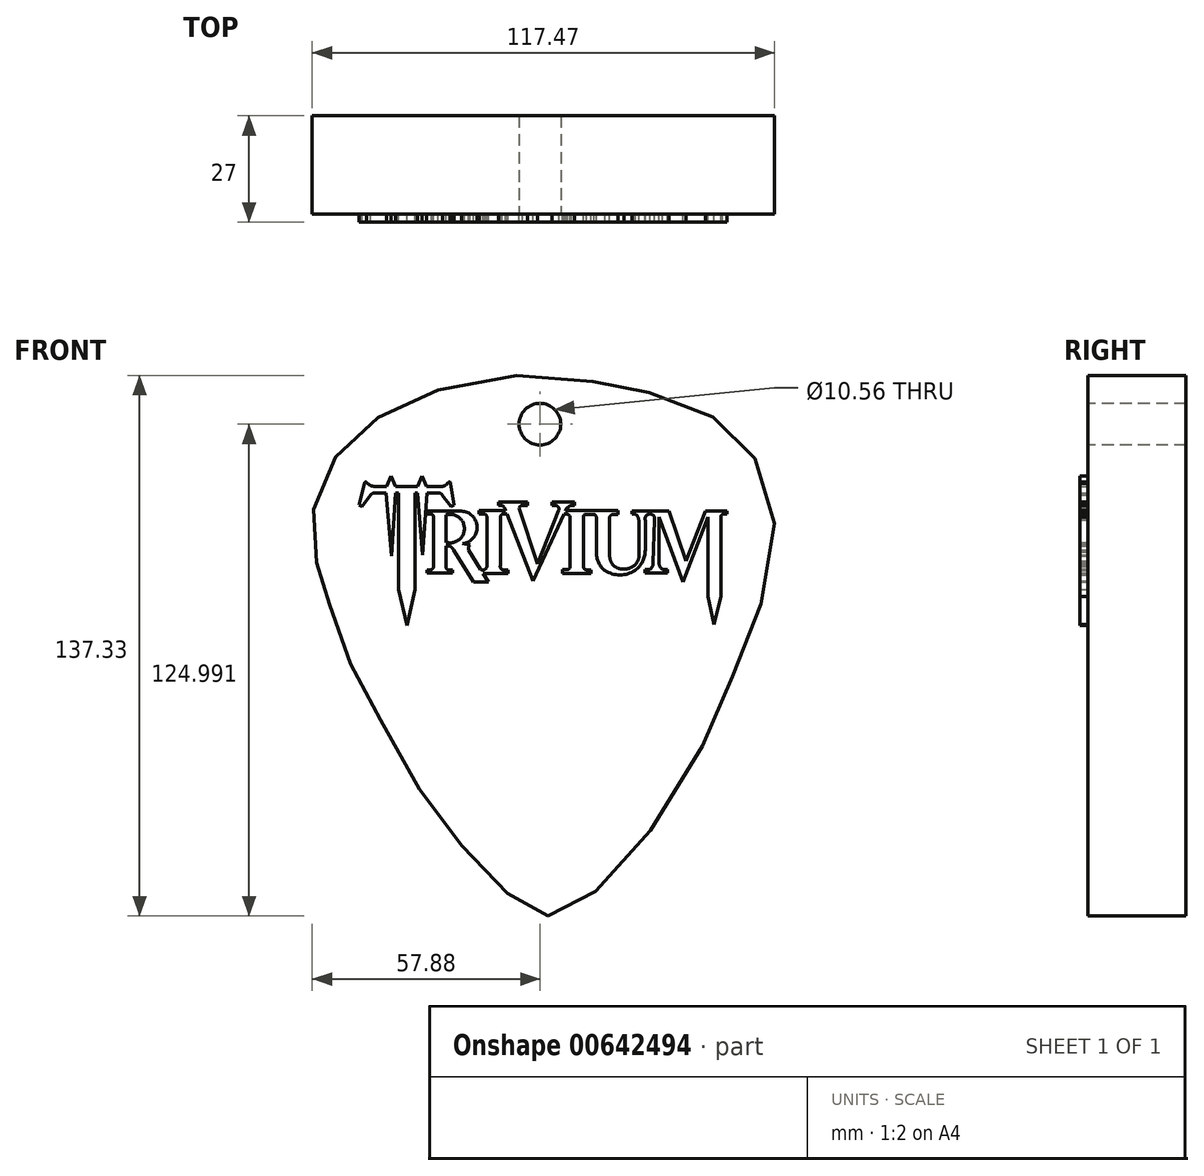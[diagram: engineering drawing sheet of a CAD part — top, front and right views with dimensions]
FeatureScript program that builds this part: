
annotation { "Feature Type Name" : "Feature", "Feature Type Description" : "" }
export const myFeature = defineFeature(function(context is Context, id is Id, definition is map)
    precondition{}
    {
        {
            var Q0;
            Q0=qCreatedBy(makeId("Front.planeOp"),FACE);
            var sketch = newSketch(context, id + "F0", { "sketchPlane" : qUnion([Q0])});
            skFitSpline(sketch, "E0", {"points": [v(1.98, -72.22) * mm, v(-3.4, -70.24) * mm, v(-13.31, -61.74) * mm, v(-24.07, -49) * mm, v(-35.12, -32.85) * mm, v(-45.03, -13.6) * mm, v(-49.85, -4.53) * mm, v(-54.38, 9.91) * mm, v(-56.15, 15.06) * mm, v(-57.8, 24.48) * mm, v(-56.74, 34.6) * mm, v(-51.16, 45.4) * mm, v(-42.15, 53.82) * mm, v(-28.73, 60.43) * mm, v(-7.1, 65.04) * mm, v(14.12, 63.43) * mm, v(25.14, 61.43) * mm, v(41.36, 56.02) * mm, v(51.37, 48.21) * mm, v(58.38, 35.8) * mm, v(58.18, 14.17) * mm, v(50.17, -8.06) * mm, v(42.96, -25.69) * mm, v(24.9, -54.7) * mm, v(10.37, -68.76) * mm, v(1.98, -72.22) * mm]});
            skSolve(sketch);
        }
        {
            var Q0;
            Q0=makeQuery(id+"F0.imprint","IMPRINT",FACE,{"disambiguationData":[TD([[makeQuery(id+"F0.imprint","IMPRINT",EDGE,{"derivedFrom":sQuery(id+"F0.wireOp",EDGE,"E0")}),-1.0]])]});
            extrude(context, id + "F1", {"entities" : qUnion([Q0]), "depth" : 25 * mm, "offsetDistance" : 25 * mm});
        }
        {
            var Q0;
            Q0=makeQuery(id+"F1.opExtrude","CAP_FACE",FACE,{"disambiguationData":[OSD([sQuery(id+"F0.wireOp",EDGE,"E0")])],"isStart":false});
            var sketch = newSketch(context, id + "F2", { "sketchPlane" : qUnion([Q0])});
            skLineSegment(sketch, "E1", {"start": v(-45.95, 32.22) * mm, "end": v(-44.6, 37.79) * mm});
            skArc(sketch, "E2", {"start": v(-44, 37.9) * mm, "mid": v(-44.33, 38.04) * mm, "end": v(-44.6, 37.79) * mm});
            skLineSegment(sketch, "E3", {"start": v(-39.02, 36.96) * mm, "end": v(-42.01, 36.96) * mm});
            skArc(sketch, "E4", {"start": v(-44, 37.9) * mm, "mid": v(-43.1, 37.2) * mm, "end": v(-42.01, 36.96) * mm});
            skLineSegment(sketch, "E5", {"start": v(-39.02, 36.96) * mm, "end": v(-37.9, 39.57) * mm});
            skLineSegment(sketch, "E6", {"start": v(-37.9, 39.57) * mm, "end": v(-36.68, 36.96) * mm});
            skLineSegment(sketch, "E7", {"start": v(-36.68, 36.96) * mm, "end": v(-31.08, 36.96) * mm});
            skLineSegment(sketch, "E8", {"start": v(-31.08, 36.96) * mm, "end": v(-30.02, 39.57) * mm});
            skLineSegment(sketch, "E9", {"start": v(-30.02, 39.57) * mm, "end": v(-28.83, 36.96) * mm});
            skLineSegment(sketch, "E10", {"start": v(-28.83, 36.96) * mm, "end": v(-24.71, 36.96) * mm});
            skLineSegment(sketch, "E11", {"start": v(-21.81, 32.16) * mm, "end": v(-22.68, 37.65) * mm});
            skFitSpline(sketch, "E12", {"points": [v(-22.68, 37.65) * mm, v(-22.79, 38) * mm, v(-23.2, 38.02) * mm, v(-23.63, 37.57) * mm, v(-23.8, 37.4) * mm, v(-24.71, 36.96) * mm], "startDerivative": vector(0, 1.24) * mm, "endDerivative": vector(-5.03, -0.55) * mm});
            skLineSegment(sketch, "E13", {"start": v(-22.56, 31.8) * mm, "end": v(-21.81, 32.16) * mm});
            skLineSegment(sketch, "E14", {"start": v(-22.56, 31.8) * mm, "end": v(-24.82, 34.79) * mm});
            skArc(sketch, "E15", {"start": v(-24.82, 34.79) * mm, "mid": v(-25.26, 35.19) * mm, "end": v(-25.85, 35.31) * mm});
            skLineSegment(sketch, "E16", {"start": v(-25.85, 35.31) * mm, "end": v(-28.72, 35.31) * mm});
            skLineSegment(sketch, "E17", {"start": v(-28.72, 35.31) * mm, "end": v(-29.77, 19.5) * mm});
            skLineSegment(sketch, "E18", {"start": v(-29.77, 19.5) * mm, "end": v(-31.15, 35.31) * mm});
            skLineSegment(sketch, "E19", {"start": v(-31.15, 35.31) * mm, "end": v(-31.8, 35.3) * mm});
            skLineSegment(sketch, "E20", {"start": v(-31.8, 35.3) * mm, "end": v(-31.8, 10.8) * mm});
            skLineSegment(sketch, "E21", {"start": v(-31.8, 10.8) * mm, "end": v(-33.71, 1.64) * mm});
            skLineSegment(sketch, "E22", {"start": v(-33.71, 1.64) * mm, "end": v(-35.97, 10.8) * mm});
            skLineSegment(sketch, "E23", {"start": v(-35.97, 10.8) * mm, "end": v(-35.97, 35.31) * mm});
            skLineSegment(sketch, "E24", {"start": v(-35.97, 35.31) * mm, "end": v(-36.72, 35.31) * mm});
            skLineSegment(sketch, "E25", {"start": v(-36.72, 35.31) * mm, "end": v(-37.75, 19.3) * mm});
            skLineSegment(sketch, "E26", {"start": v(-37.75, 19.3) * mm, "end": v(-39.1, 35.31) * mm});
            skLineSegment(sketch, "E27", {"start": v(-39.1, 35.31) * mm, "end": v(-41.92, 35.31) * mm});
            skArc(sketch, "E28", {"start": v(-41.92, 35.31) * mm, "mid": v(-42.51, 35.17) * mm, "end": v(-42.98, 34.79) * mm});
            skLineSegment(sketch, "E29", {"start": v(-45.16, 31.89) * mm, "end": v(-42.98, 34.79) * mm});
            skLineSegment(sketch, "E30", {"start": v(-45.95, 32.22) * mm, "end": v(-45.16, 31.89) * mm});
            skLineSegment(sketch, "E31", {"start": v(-28.63, 30.67) * mm, "end": v(-28.63, 29.97) * mm});
            skLineSegment(sketch, "E32", {"start": v(-28.63, 30.67) * mm, "end": v(-19.94, 30.67) * mm});
            skArc(sketch, "E33", {"start": v(-19.64, 22.41) * mm, "mid": v(-15.97, 26.68) * mm, "end": v(-19.94, 30.67) * mm});
            skLineSegment(sketch, "E34", {"start": v(-13.11, 12.71) * mm, "end": v(-16.94, 12.71) * mm});
            skLineSegment(sketch, "E35", {"start": v(-23.05, 21.85) * mm, "end": v(-23.9, 21.85) * mm});
            skLineSegment(sketch, "E36", {"start": v(-23.9, 21.85) * mm, "end": v(-23.9, 16.48) * mm});
            skArc(sketch, "E37", {"start": v(-23.9, 16.48) * mm, "mid": v(-23.6, 15.9) * mm, "end": v(-22.96, 15.74) * mm});
            skLineSegment(sketch, "E38", {"start": v(-23.88, 29.7) * mm, "end": v(-23.88, 22.76) * mm});
            skArc(sketch, "E39", {"start": v(-23.88, 22.76) * mm, "mid": v(-19.19, 26.23) * mm, "end": v(-23.88, 29.7) * mm});
            skLineSegment(sketch, "E40", {"start": v(-19.64, 22.41) * mm, "end": v(-17.71, 22.11) * mm});
            skArc(sketch, "E41", {"start": v(-17.71, 22.11) * mm, "mid": v(-18.12, 21.5) * mm, "end": v(-18.12, 20.78) * mm});
            skLineSegment(sketch, "E42", {"start": v(-18.12, 20.78) * mm, "end": v(-15.08, 15.84) * mm});
            skArc(sketch, "E43", {"start": v(-15.08, 15.84) * mm, "mid": v(-14.07, 15.82) * mm, "end": v(-13.46, 16.61) * mm});
            skLineSegment(sketch, "E44", {"start": v(-14.48, 14.84) * mm, "end": v(-13.11, 12.71) * mm});
            skLineSegment(sketch, "E45", {"start": v(-14.48, 14.84) * mm, "end": v(-8.17, 14.84) * mm});
            skLineSegment(sketch, "E46", {"start": v(-16.94, 12.71) * mm, "end": v(-21.93, 20.84) * mm});
            skArc(sketch, "E47", {"start": v(-21.93, 20.84) * mm, "mid": v(-22.42, 21.43) * mm, "end": v(-23.05, 21.85) * mm});
            skLineSegment(sketch, "E48", {"start": v(-22.96, 15.74) * mm, "end": v(-22.16, 15.74) * mm});
            skLineSegment(sketch, "E49", {"start": v(-22.16, 15.74) * mm, "end": v(-22.16, 14.96) * mm});
            skLineSegment(sketch, "E50", {"start": v(-22.16, 14.96) * mm, "end": v(-28.66, 14.96) * mm});
            skLineSegment(sketch, "E51", {"start": v(-28.66, 14.96) * mm, "end": v(-28.66, 15.74) * mm});
            skLineSegment(sketch, "E52", {"start": v(-28.66, 15.74) * mm, "end": v(-27.93, 15.74) * mm});
            skArc(sketch, "E53", {"start": v(-27.93, 15.74) * mm, "mid": v(-27.33, 15.98) * mm, "end": v(-27.04, 16.56) * mm});
            skLineSegment(sketch, "E54", {"start": v(-27.04, 16.56) * mm, "end": v(-27.04, 29.12) * mm});
            skArc(sketch, "E55", {"start": v(-27.04, 29.12) * mm, "mid": v(-27.17, 29.58) * mm, "end": v(-27.51, 29.9) * mm});
            skLineSegment(sketch, "E56", {"start": v(-28.63, 29.97) * mm, "end": v(-28.63, 29.9) * mm});
            skLineSegment(sketch, "E57", {"start": v(-28.63, 29.9) * mm, "end": v(-27.51, 29.9) * mm});
            skLineSegment(sketch, "E58", {"start": v(-13.46, 16.61) * mm, "end": v(-13.46, 29.1) * mm});
            skLineSegment(sketch, "E59", {"start": v(-8.17, 14.84) * mm, "end": v(-8.17, 15.68) * mm});
            skLineSegment(sketch, "E60", {"start": v(-8.17, 15.68) * mm, "end": v(-9.16, 15.68) * mm});
            skArc(sketch, "E61", {"start": v(-10.06, 16.84) * mm, "mid": v(-9.89, 16.04) * mm, "end": v(-9.16, 15.68) * mm});
            skLineSegment(sketch, "E62", {"start": v(-10.06, 16.84) * mm, "end": v(-10.06, 28.89) * mm});
            skArc(sketch, "E63", {"start": v(-13.46, 29.1) * mm, "mid": v(-13.6, 29.58) * mm, "end": v(-14, 29.9) * mm});
            skArc(sketch, "E64", {"start": v(-9.58, 29.89) * mm, "mid": v(-9.97, 29.46) * mm, "end": v(-10.06, 28.89) * mm});
            skLineSegment(sketch, "E65", {"start": v(-14, 29.9) * mm, "end": v(-15.5, 29.9) * mm});
            skLineSegment(sketch, "E66", {"start": v(-15.5, 29.9) * mm, "end": v(-15.5, 30.77) * mm});
            skLineSegment(sketch, "E67", {"start": v(-15.5, 30.77) * mm, "end": v(-8.74, 30.77) * mm});
            skLineSegment(sketch, "E68", {"start": v(-8.39, 29.9) * mm, "end": v(-9.58, 29.89) * mm});
            skLineSegment(sketch, "E69", {"start": v(-10.58, 32.13) * mm, "end": v(-9.62, 32.13) * mm});
            skArc(sketch, "E70", {"start": v(-8.74, 30.77) * mm, "mid": v(-9.03, 31.54) * mm, "end": v(-9.62, 32.13) * mm});
            skLineSegment(sketch, "E71", {"start": v(-10.58, 32.13) * mm, "end": v(-10.58, 33) * mm});
            skLineSegment(sketch, "E72", {"start": v(-8.39, 29.9) * mm, "end": v(-1.8, 12.87) * mm});
            skLineSegment(sketch, "E73", {"start": v(-1.8, 12.87) * mm, "end": v(6.05, 29.89) * mm});
            skArc(sketch, "E74", {"start": v(-4.42, 32.12) * mm, "mid": v(-4.94, 31.93) * mm, "end": v(-5.27, 31.5) * mm});
            skLineSegment(sketch, "E75", {"start": v(-4.42, 32.12) * mm, "end": v(-3.12, 32.12) * mm});
            skLineSegment(sketch, "E76", {"start": v(-3.12, 32.12) * mm, "end": v(-3.12, 33.04) * mm});
            skLineSegment(sketch, "E77", {"start": v(-3.12, 33.04) * mm, "end": v(-10.58, 33) * mm});
            skLineSegment(sketch, "E78", {"start": v(-5.27, 31.5) * mm, "end": v(-0.66, 17.23) * mm});
            skLineSegment(sketch, "E79", {"start": v(-0.66, 17.23) * mm, "end": v(4.75, 30.77) * mm});
            skArc(sketch, "E80", {"start": v(4.75, 30.77) * mm, "mid": v(4.64, 31.7) * mm, "end": v(3.8, 32.13) * mm});
            skLineSegment(sketch, "E81", {"start": v(3.08, 32.12) * mm, "end": v(3.8, 32.13) * mm});
            skLineSegment(sketch, "E82", {"start": v(3.08, 32.12) * mm, "end": v(3.07, 32.97) * mm});
            skLineSegment(sketch, "E83", {"start": v(3.07, 32.97) * mm, "end": v(8.84, 32.97) * mm});
            skLineSegment(sketch, "E84", {"start": v(8.84, 32.97) * mm, "end": v(8.84, 32.12) * mm});
            skLineSegment(sketch, "E85", {"start": v(8.84, 32.12) * mm, "end": v(8, 32.12) * mm});
            skArc(sketch, "E86", {"start": v(8, 32.12) * mm, "mid": v(7.1, 31.64) * mm, "end": v(6.5, 30.81) * mm});
            skLineSegment(sketch, "E87", {"start": v(6.5, 30.81) * mm, "end": v(19.8, 30.81) * mm});
            skLineSegment(sketch, "E88", {"start": v(19.8, 30.81) * mm, "end": v(19.8, 29.85) * mm});
            skLineSegment(sketch, "E89", {"start": v(19.8, 29.85) * mm, "end": v(18.78, 29.85) * mm});
            skArc(sketch, "E90", {"start": v(18.78, 29.85) * mm, "mid": v(18.15, 29.68) * mm, "end": v(17.71, 29.2) * mm});
            skLineSegment(sketch, "E91", {"start": v(17.71, 29.2) * mm, "end": v(17.71, 19.24) * mm});
            skArc(sketch, "E92", {"start": v(17.71, 19.24) * mm, "mid": v(18.8, 16.78) * mm, "end": v(21.37, 15.94) * mm});
            skArc(sketch, "E93", {"start": v(21.37, 15.94) * mm, "mid": v(24.1, 17.02) * mm, "end": v(25.22, 19.72) * mm});
            skLineSegment(sketch, "E94", {"start": v(25.1, 28.28) * mm, "end": v(25.22, 19.72) * mm});
            skArc(sketch, "E95", {"start": v(25.1, 28.28) * mm, "mid": v(24.87, 29.21) * mm, "end": v(24.22, 29.93) * mm});
            skLineSegment(sketch, "E96", {"start": v(23.32, 29.93) * mm, "end": v(24.22, 29.93) * mm});
            skLineSegment(sketch, "E97", {"start": v(23.32, 29.93) * mm, "end": v(23.32, 30.76) * mm});
            skLineSegment(sketch, "E98", {"start": v(23.32, 30.76) * mm, "end": v(32.83, 30.76) * mm});
            skArc(sketch, "E99", {"start": v(29.12, 28.46) * mm, "mid": v(27.88, 29.92) * mm, "end": v(26.75, 28.38) * mm});
            skLineSegment(sketch, "E100", {"start": v(26.75, 28.38) * mm, "end": v(26.75, 20.77) * mm});
            skLineSegment(sketch, "E101", {"start": v(29.12, 28.46) * mm, "end": v(28.76, 17.46) * mm});
            skArc(sketch, "E102", {"start": v(24.14, 15.54) * mm, "mid": v(26.06, 17.84) * mm, "end": v(26.75, 20.77) * mm});
            skArc(sketch, "E103", {"start": v(16.5, 15.54) * mm, "mid": v(20.32, 14.47) * mm, "end": v(24.14, 15.54) * mm});
            skArc(sketch, "E104", {"start": v(14.36, 20.32) * mm, "mid": v(14.88, 17.69) * mm, "end": v(16.5, 15.54) * mm});
            skLineSegment(sketch, "E105", {"start": v(14.36, 20.32) * mm, "end": v(14.36, 28.87) * mm});
            skArc(sketch, "E106", {"start": v(14.36, 28.87) * mm, "mid": v(14.2, 29.46) * mm, "end": v(13.73, 29.87) * mm});
            skLineSegment(sketch, "E107", {"start": v(13.73, 29.87) * mm, "end": v(11.63, 29.87) * mm});
            skArc(sketch, "E108", {"start": v(11.63, 29.87) * mm, "mid": v(11.23, 29.7) * mm, "end": v(11.05, 29.31) * mm});
            skLineSegment(sketch, "E109", {"start": v(11.05, 29.31) * mm, "end": v(11.05, 16.52) * mm});
            skLineSegment(sketch, "E110", {"start": v(6.05, 29.89) * mm, "end": v(6.83, 29.89) * mm});
            skArc(sketch, "E111", {"start": v(7.67, 29.2) * mm, "mid": v(7.37, 29.7) * mm, "end": v(6.83, 29.89) * mm});
            skLineSegment(sketch, "E112", {"start": v(7.67, 29.2) * mm, "end": v(7.67, 16.68) * mm});
            skArc(sketch, "E113", {"start": v(7.06, 15.78) * mm, "mid": v(7.5, 16.13) * mm, "end": v(7.67, 16.68) * mm});
            skArc(sketch, "E114", {"start": v(11.05, 16.52) * mm, "mid": v(11.27, 16) * mm, "end": v(11.8, 15.75) * mm});
            skLineSegment(sketch, "E115", {"start": v(7.06, 15.78) * mm, "end": v(5.75, 15.78) * mm});
            skLineSegment(sketch, "E116", {"start": v(5.75, 15.78) * mm, "end": v(5.75, 14.84) * mm});
            skLineSegment(sketch, "E117", {"start": v(5.75, 14.84) * mm, "end": v(12.95, 14.84) * mm});
            skLineSegment(sketch, "E118", {"start": v(12.95, 14.84) * mm, "end": v(12.95, 15.76) * mm});
            skLineSegment(sketch, "E119", {"start": v(12.95, 15.76) * mm, "end": v(11.8, 15.75) * mm});
            skArc(sketch, "E120", {"start": v(27.9, 15.8) * mm, "mid": v(28.52, 16.53) * mm, "end": v(28.76, 17.46) * mm});
            skLineSegment(sketch, "E121", {"start": v(27.9, 15.8) * mm, "end": v(26.62, 15.8) * mm});
            skLineSegment(sketch, "E122", {"start": v(26.62, 15.8) * mm, "end": v(26.62, 14.96) * mm});
            skLineSegment(sketch, "E123", {"start": v(26.62, 14.96) * mm, "end": v(32.38, 14.96) * mm});
            skLineSegment(sketch, "E124", {"start": v(32.38, 14.96) * mm, "end": v(32.38, 15.8) * mm});
            skLineSegment(sketch, "E125", {"start": v(32.38, 15.8) * mm, "end": v(31.17, 15.8) * mm});
            skArc(sketch, "E126", {"start": v(30.21, 17.68) * mm, "mid": v(30.49, 16.63) * mm, "end": v(31.17, 15.8) * mm});
            skLineSegment(sketch, "E127", {"start": v(30.21, 17.68) * mm, "end": v(30.21, 29.2) * mm});
            skLineSegment(sketch, "E128", {"start": v(30.21, 29.2) * mm, "end": v(36.35, 12.62) * mm});
            skLineSegment(sketch, "E129", {"start": v(36.35, 12.62) * mm, "end": v(42.72, 29.2) * mm});
            skLineSegment(sketch, "E130", {"start": v(42.72, 29.2) * mm, "end": v(42.72, 9.02) * mm});
            skLineSegment(sketch, "E131", {"start": v(42.72, 9.02) * mm, "end": v(44.26, 1.88) * mm});
            skLineSegment(sketch, "E132", {"start": v(44.26, 1.88) * mm, "end": v(45.96, 9.02) * mm});
            skLineSegment(sketch, "E133", {"start": v(45.96, 9.02) * mm, "end": v(45.96, 29.2) * mm});
            skArc(sketch, "E134", {"start": v(46.41, 29.88) * mm, "mid": v(46.1, 29.6) * mm, "end": v(45.96, 29.2) * mm});
            skLineSegment(sketch, "E135", {"start": v(46.41, 29.88) * mm, "end": v(47.5, 29.88) * mm});
            skLineSegment(sketch, "E136", {"start": v(47.5, 29.88) * mm, "end": v(47.5, 30.7) * mm});
            skLineSegment(sketch, "E137", {"start": v(47.5, 30.7) * mm, "end": v(42.02, 30.7) * mm});
            skLineSegment(sketch, "E138", {"start": v(42.02, 30.7) * mm, "end": v(37.13, 18) * mm});
            skLineSegment(sketch, "E139", {"start": v(37.13, 18) * mm, "end": v(32.83, 30.76) * mm});
            skSolve(sketch);
        }
        {
            var Q0;
            Q0 = qSketchRegion(id + "F2", true);
            extrude(context, id + "F3", {"entities" : qUnion([Q0]), "operationType" : NewBodyOperationType.ADD, "depth" : 2 * mm, "offsetDistance" : 25 * mm});
        }
        {
            var Q0;
            Q0=makeQuery(id+"F2.imprint","IMPRINT",FACE,{"disambiguationData":[TD([[makeQuery(id+"F2.imprint","IMPRINT",EDGE,{"derivedFrom":sQuery(id+"F2.wireOp",EDGE,"E1")}),1.0]])]});
            var sketch = newSketch(context, id + "F4", { "sketchPlane" : qUnion([Q0])});
            skCircle(sketch, "E140", {"center": v(0, 52.77) * mm, "radius": 5.28 * mm});
            skSolve(sketch);
        }
        {
            var Q0;
            Q0=makeQuery(id+"F4.imprint","IMPRINT",FACE,{"disambiguationData":[TD([[makeQuery(id+"F4.imprint","IMPRINT",EDGE,{"derivedFrom":sQuery(id+"F4.wireOp",EDGE,"E140")}),1.0]])]});
            var Q1;
            Q1=sQuery(id+"F4.wireOp",EDGE,"E140");
            extrude(context, id + "F5", {"entities" : qUnion([Q0]), "operationType" : NewBodyOperationType.REMOVE, "surfaceEntities" : qUnion([Q1]), "endBound" : BoundingType.UP_TO_NEXT, "oppositeDirection" : true, "depth" : 25 * mm, "offsetDistance" : 25 * mm});
        }
    });
